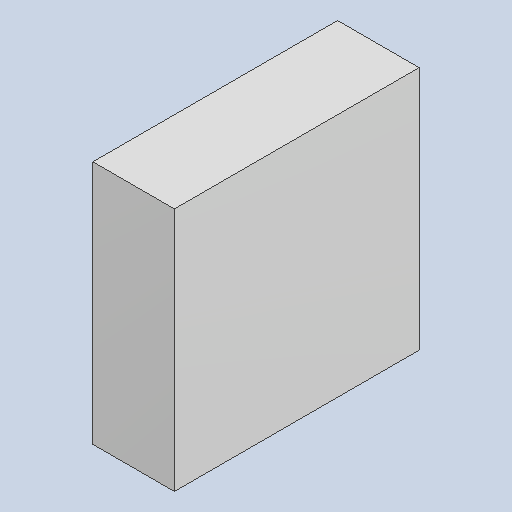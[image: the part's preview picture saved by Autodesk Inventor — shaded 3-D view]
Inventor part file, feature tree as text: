
AUTODESK INVENTOR PART (.ipt)
format: ipt  version: 2023.4 (Build 274418000, 418)  size: 81,408 bytes
history: native  units: mm
features: extrude x1
ambient origin geometry x8: Origin, YZ Plane, XZ Plane, XY Plane, X Axis, Y Axis, Z Axis, Center Point
bodies: Solid1 (feature_tree)
feature tree (1):
  extrude  "Extruded_8"  [1 undecoded]
note: 1 required parameter value undecoded (feature->parameter linkage not recoverable at this tier; creation-order binding heuristic only, values carry confidence <= 0.55)
